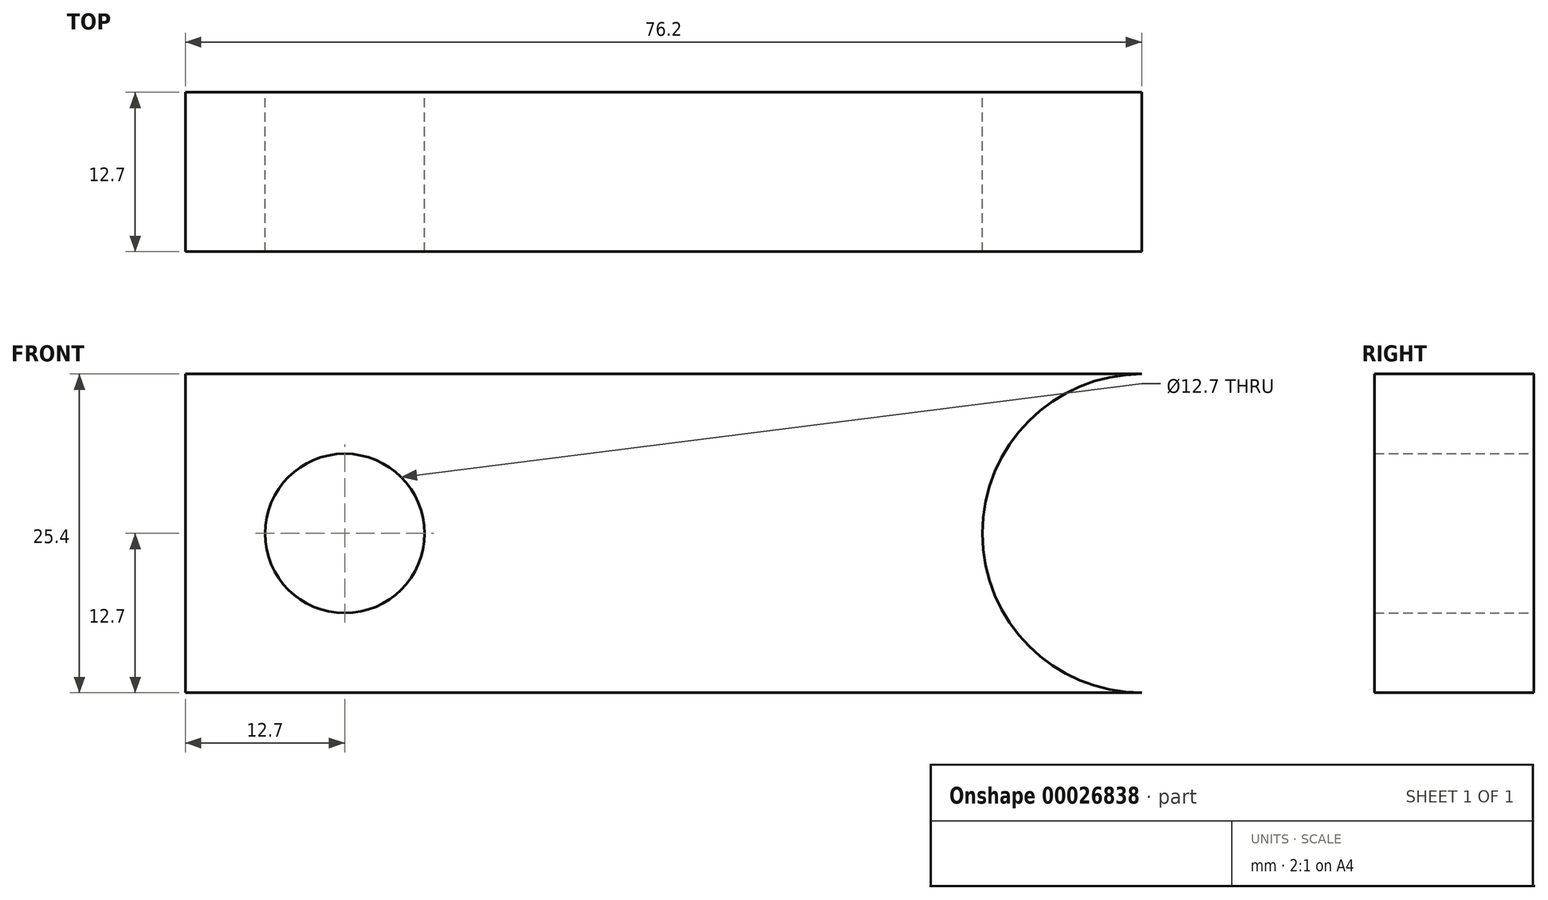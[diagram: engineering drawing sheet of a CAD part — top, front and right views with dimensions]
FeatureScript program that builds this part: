
annotation { "Feature Type Name" : "Feature", "Feature Type Description" : "" }
export const myFeature = defineFeature(function(context is Context, id is Id, definition is map)
    precondition{}
    {
        {
            var Q0;
            Q0=qCreatedBy(makeId("Front.planeOp"),FACE);
            var sketch = newSketch(context, id + "F0", { "sketchPlane" : qUnion([Q0])});
            skLineSegment(sketch, "E0.bottom", {"start": v(0, 0) * mm, "end": v(76.2, 0) * mm});
            skLineSegment(sketch, "E0.top", {"start": v(0, 25.4) * mm, "end": v(76.2, 25.4) * mm});
            skLineSegment(sketch, "E0.left", {"start": v(0, 0) * mm, "end": v(0, 25.4) * mm});
            skPoint(sketch, "E1", {"position": v(0, 12.7) * mm});
            skPoint(sketch, "E2", {"position": v(12.7, 12.7) * mm});
            skCircle(sketch, "E3", {"center": v(12.7, 12.7) * mm, "radius": 6.35 * mm});
            skPoint(sketch, "E4", {"position": v(76.2, 12.7) * mm});
            skArc(sketch, "E5", {"start": v(76.2, 25.4) * mm, "mid": v(63.5, 12.7) * mm, "end": v(76.2, 0) * mm});
            skSolve(sketch);
        }
        {
            var Q0;
            Q0 = qSketchRegion(id + "F0", true);
            extrude(context, id + "F1", {"entities" : qUnion([Q0]), "depth" : 12.7 * mm});
        }
    });
